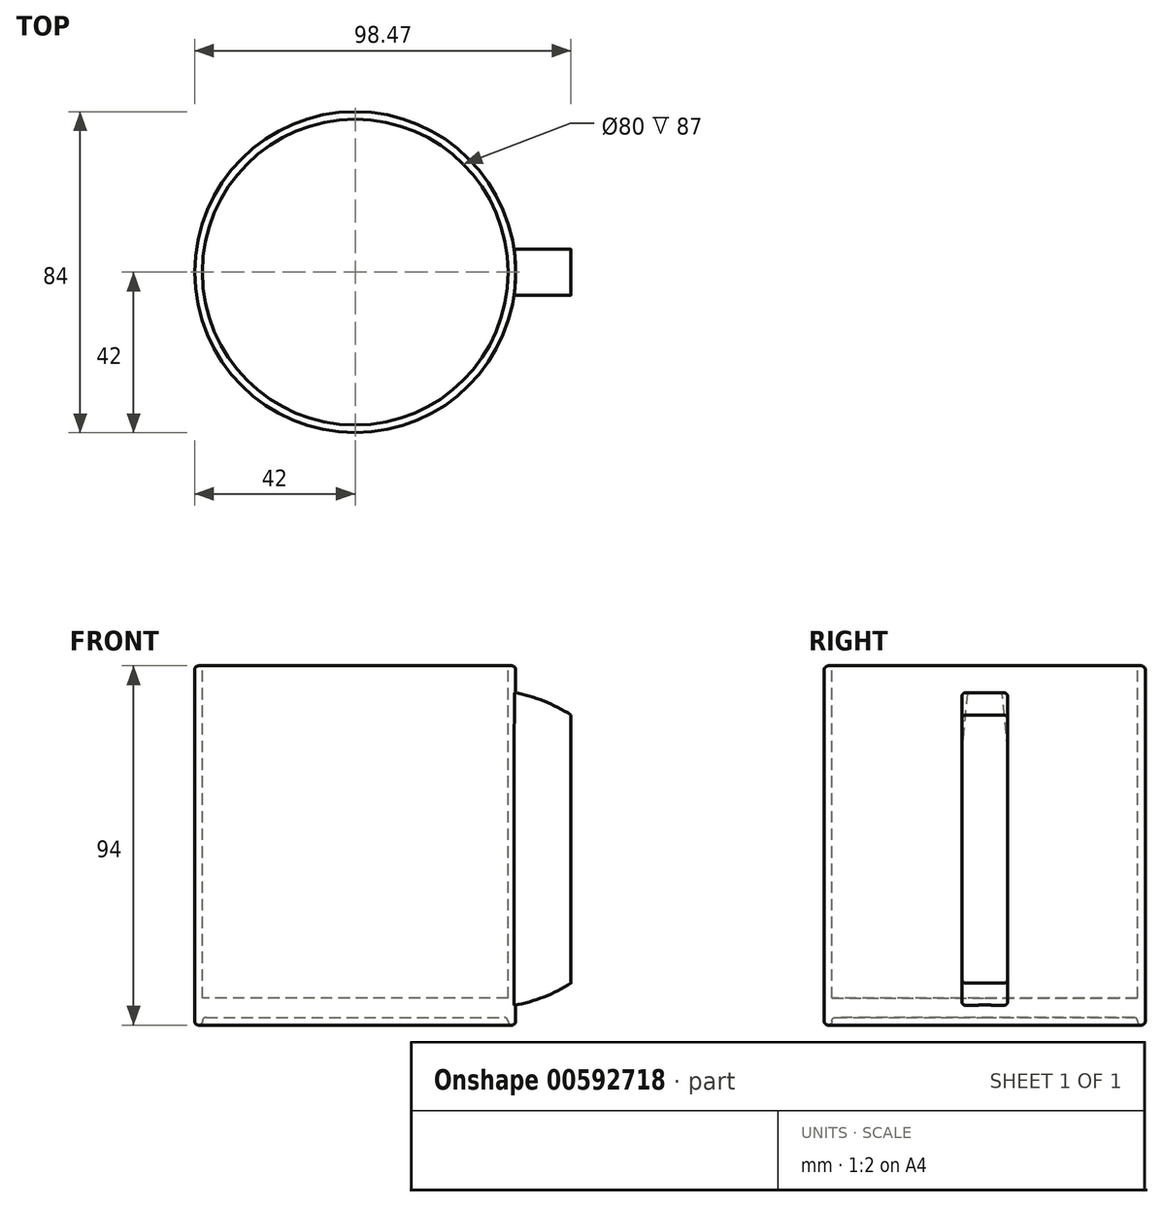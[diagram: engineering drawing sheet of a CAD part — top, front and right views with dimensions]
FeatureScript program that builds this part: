
annotation { "Feature Type Name" : "Feature", "Feature Type Description" : "" }
export const myFeature = defineFeature(function(context is Context, id is Id, definition is map)
    precondition{}
    {
        {
            var Q0;
            Q0=qCreatedBy(makeId("Top.planeOp"),FACE);
            var sketch = newSketch(context, id + "F0", { "sketchPlane" : qUnion([Q0])});
            skCircle(sketch, "E0", {"center": v(0, 0) * mm, "radius": 42 * mm});
            skSolve(sketch);
        }
        {
            var Q0;
            Q0=makeQuery(id+"F0.imprint","IMPRINT",FACE,{"disambiguationData":[TD([[makeQuery(id+"F0.imprint","IMPRINT",EDGE,{"derivedFrom":sQuery(id+"F0.wireOp",EDGE,"E0")}),1.0]])]});
            var Q1;
            Q1 = qSketchRegion(id + "F2", true);
            extrude(context, id + "F1", {"entities" : qUnion([Q0, Q1]), "depth" : 94 * mm, "offsetDistance" : 25 * mm});
        }
        {
            var Q0;
            Q0=makeQuery(id+"F1.opExtrude","CAP_FACE",FACE,{"disambiguationData":[OSD([sQuery(id+"F0.wireOp",EDGE,"E0")])],"isStart":false});
            var sketch = newSketch(context, id + "F2", { "sketchPlane" : qUnion([Q0])});
            skCircle(sketch, "E1", {"center": v(0, 0) * mm, "radius": 40 * mm});
            skSolve(sketch);
        }
        {
            var Q0;
            Q0 = qSketchRegion(id + "F2", true);
            extrude(context, id + "F3", {"entities" : qUnion([Q0]), "operationType" : NewBodyOperationType.REMOVE, "oppositeDirection" : true, "depth" : 87 * mm, "offsetDistance" : 25 * mm});
        }
        {
            var Q0;
            Q0=makeQuery(id+"F1.opExtrude","CAP_EDGE",EDGE,{"disambiguationData":[OSD([sQuery(id+"F0.wireOp",EDGE,"E0")])],"isStart":false});
            var Q1;
            Q1=makeQuery(id+"F3.boolean.opBoolean","COPY",EDGE,{"derivedFrom":makeQuery(id+"F3.opExtrude","CAP_EDGE",EDGE,{"disambiguationData":[OSD([sQuery(id+"F2.wireOp",EDGE,"E1")])],"isStart":true})});
            var Q2;
            Q2=makeQuery(id+"F1.opExtrude","CAP_EDGE",EDGE,{"disambiguationData":[OSD([sQuery(id+"F0.wireOp",EDGE,"E0")])],"isStart":true});
            fillet(context, id + "F4", {"entities" : qUnion([Q0, Q1, Q2]), "radius" : 1 * mm, "tangentPropagation" : true, "allowEdgeOverflow" : false});
        }
        {
            var Q0;
            Q0=qCreatedBy(makeId("Front.planeOp"),FACE);
            var sketch = newSketch(context, id + "F5", { "sketchPlane" : qUnion([Q0])});
            skPoint(sketch, "E2", {"position": v(56.47, 0) * mm});
            skLineSegment(sketch, "E3", {"start": v(56.47, 0) * mm, "end": v(56.47, 92) * mm});
            skPoint(sketch, "E4", {"position": v(56.47, 76) * mm});
            skPoint(sketch, "E5", {"position": v(56.47, 16) * mm});
            skLineSegment(sketch, "E6", {"start": v(56.47, 76) * mm, "end": v(56.47, 92) * mm});
            skLineSegment(sketch, "E7", {"start": v(56.47, 16) * mm, "end": v(56.47, 0) * mm});
            skPoint(sketch, "E8", {"position": v(41.82, 92.26) * mm});
            skPoint(sketch, "E9", {"position": v(40.7, 0) * mm});
            skPoint(sketch, "E10", {"position": v(40.7, 16) * mm});
            skPoint(sketch, "E11", {"position": v(40.7, 76) * mm});
            skLineSegment(sketch, "E12", {"start": v(56.47, 92) * mm, "end": v(56.47, 76) * mm});
            skPoint(sketch, "E13", {"position": v(56.47, 87) * mm});
            skPoint(sketch, "E14", {"position": v(56.47, 5) * mm});
            skLineSegment(sketch, "E15", {"start": v(56.47, 87) * mm, "end": v(56.47, 92) * mm});
            skLineSegment(sketch, "E16", {"start": v(56.47, 5) * mm, "end": v(56.47, 0) * mm});
            skPoint(sketch, "E17", {"position": v(41.48, 87) * mm});
            skPoint(sketch, "E18", {"position": v(56.47, 46) * mm});
            skLineSegment(sketch, "E19", {"start": v(56.47, 46) * mm, "end": v(56.47, 92) * mm});
            skPoint(sketch, "E20", {"position": v(75.74, 46) * mm});
            skCircle(sketch, "E21", {"center": v(34.15, 46.07) * mm, "radius": 41.58 * mm});
            skPoint(sketch, "E21.third.point", {"position": v(40.7, 5) * mm});
            skLineSegment(sketch, "E22", {"start": v(41.82, 92.26) * mm, "end": v(40.7, 0) * mm});
            skCircle(sketch, "E23", {"center": v(34.15, 46.07) * mm, "radius": 37.1 * mm});
            skSolve(sketch);
        }
        {
            var Q0;
            {var subQ0=sQuery(id+"F5.wireOp",EDGE,"E19");var subQ1=makeQuery(id+"F5.imprint","IMPRINT",VERTEX,{"derivedFrom":subQ0});Q0=makeQuery(id+"F5.imprint","IMPRINT",FACE,{"disambiguationData":[TD([[makeQuery(id+"F5.imprint","IMPRINT",EDGE,{"disambiguationData":[TD([[subQ1,1.0]])],"derivedFrom":subQ0}),-1.0]])]});}
            var Q1;
            {var subQ1=sQuery(id+"F5.wireOp",EDGE,"E7");var subQ7=sQuery(id+"F5.wireOp",EDGE,"E3");var subQ8=makeQuery(id+"F5.imprint","INTERSECT",VERTEX,{"derivedFrom":[subQ7,subQ1]});Q1=makeQuery(id+"F5.imprint","IMPRINT",FACE,{"disambiguationData":[TD([[makeQuery(id+"F5.imprint","IMPRINT",EDGE,{"disambiguationData":[TD([[subQ8,-1.0]])],"derivedFrom":subQ7}),1.0]])]});}
            var Q2;
            {var subQ1=sQuery(id+"F5.wireOp",EDGE,"E19");var subQ7=makeQuery(id+"F5.imprint","IMPRINT",VERTEX,{"derivedFrom":subQ1});Q2=makeQuery(id+"F5.imprint","IMPRINT",FACE,{"disambiguationData":[TD([[makeQuery(id+"F5.imprint","IMPRINT",EDGE,{"disambiguationData":[TD([[subQ7,1.0]])],"derivedFrom":subQ1}),1.0]])]});}
            extrude(context, id + "F6", {"entities" : qUnion([Q0, Q1, Q2]), "operationType" : NewBodyOperationType.ADD, "endBound" : BoundingType.SYMMETRIC, "depth" : 12 * mm, "offsetDistance" : 25 * mm});
        }
        {
            var Q0;
            Q0=makeQuery(id+"F6.opExtrude","CAP_EDGE",EDGE,{"disambiguationData":[OSD([sQuery(id+"F5.wireOp",EDGE,"E21")])],"isStart":false});
            var Q1;
            Q1=makeQuery(id+"F6.opExtrude","CAP_EDGE",EDGE,{"disambiguationData":[OSD([sQuery(id+"F5.wireOp",EDGE,"E23")])],"isStart":false});
            var Q2;
            Q2=makeQuery(id+"F6.opExtrude","CAP_EDGE",EDGE,{"disambiguationData":[OSD([sQuery(id+"F5.wireOp",EDGE,"E23")])],"isStart":true});
            var Q3;
            Q3=makeQuery(id+"F6.opExtrude","CAP_EDGE",EDGE,{"disambiguationData":[OSD([sQuery(id+"F5.wireOp",EDGE,"E21")])],"isStart":true});
            fillet(context, id + "F7", {"entities" : qUnion([Q0, Q1, Q2, Q3]), "radius" : 1 * mm, "tangentPropagation" : true, "allowEdgeOverflow" : false});
        }
        {
            var Q0;
            Q0=makeQuery(id+"F1.opExtrude","CAP_FACE",FACE,{"disambiguationData":[OSD([sQuery(id+"F0.wireOp",EDGE,"E0")])],"isStart":true});
            var sketch = newSketch(context, id + "F8", { "sketchPlane" : qUnion([Q0])});
            skCircle(sketch, "E24", {"center": v(0, 0) * mm, "radius": 40 * mm});
            skSolve(sketch);
        }
        {
            var Q0;
            Q0 = qSketchRegion(id + "F8", true);
            extrude(context, id + "F9", {"entities" : qUnion([Q0]), "operationType" : NewBodyOperationType.REMOVE, "oppositeDirection" : true, "depth" : 2 * mm, "offsetDistance" : 25 * mm});
        }
        {
            var Q0;
            Q0=makeQuery(id+"F9.boolean.opBoolean","COPY",FACE,{"derivedFrom":makeQuery(id+"F9.opExtrude","SWEPT_FACE",FACE,{"disambiguationData":[OSD([sQuery(id+"F8.wireOp",EDGE,"E24")])]})});
            fillet(context, id + "F10", {"entities" : qUnion([Q0]), "radius" : 1 * mm, "tangentPropagation" : true, "allowEdgeOverflow" : false});
        }
    });
